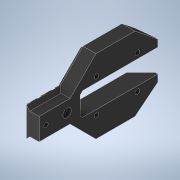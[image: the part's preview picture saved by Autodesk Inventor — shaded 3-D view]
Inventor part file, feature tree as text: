
AUTODESK INVENTOR PART (.ipt)
format: ipt  version: 2021 (Build 250183000, 183)  size: 281,600 bytes
history: native  units: mm
features: extrude x7, sketch x6, chamfer x3, projected_geometry x3, pattern_linear x1
ambient origin geometry x8: Origin, YZ Plane, XZ Plane, XY Plane, X Axis, Y Axis, Z Axis, Center Point
bodies: Solid1 (feature_tree)
feature tree (20):
  extrude  "Extrusion1"  Depth=29.0mm
  extrude  "Extrusion2"  Depth=12.0mm
  chamfer  "Chamfer3"  Distance=55.2mm
  chamfer  "Chamfer2"  Distance=29.2mm
  extrude  "Extrusion3"  Depth=10.0mm
  extrude  "Extrusion4"  Depth=10.0mm
  pattern_linear  "Rectangular Pattern1"  Spacing1=12.0mm  [1 undecoded]
  sketch  "Sketch5"  dims[d6=1.85mm]
  extrude  "Extrusion5"  Depth=18.0mm
  extrude  "Extrusion6"  Depth=10.0mm
  extrude  "Extrusion7"  Depth=10.0mm
  chamfer  "Chamfer5"  Distance=15.6718mm
  sketch  "Sketch1"  dims[d0=24.0mm d1=29.0mm]
  sketch  "Sketch2"  dims[d2=16.5mm d3=12.0mm]
  sketch  "Sketch3"  dims[d4=3.2mm]
  projected_geometry  "Projected Loop1"
  projected_geometry  "Projected Loop2"
  sketch  "Sketch4"  dims[d5=11.8mm]
  sketch  "Sketch6"  dims[d7=1.85mm d9=55.2mm d11=29.2mm d12=25.967009mm d13=32.0mm d14=12.0mm d15=0.0mm d16=18.0mm d17=5.0mm d19=24.668484mm d23=15.6718mm d29=15.67mm d30=2.76mm d32=10.15mm d33=2.77mm d34=2.77mm d35=3.78mm d36=0.0mm d37=20.0mm d38=80.0mm d40=22.0mm d41=0.0mm d42=2.77mm d43=2.0mm d44=45.0deg d45=18.41498mm d46=2.0mm d47=45.0deg d51=0.0mm d52=0.0mm d56=5.25mm d58=4.0mm d59=0.0mm d60=0.0mm d61=30.0mm d63=10.0mm d64=1.0mm d65=18.0mm d66=5.0mm d67=20.0mm d68=6.0mm d69=3.2mm d70=3.0mm d71=0.0mm d72=0.0mm d73=0.0mm d74=6.0mm d75=9.0mm d76=0.0mm d77=10.0mm d78=2.0mm d79=45.0deg]
  projected_geometry  "Projected Loop3"
note: 1 required parameter value undecoded (feature->parameter linkage not recoverable at this tier; creation-order binding heuristic only, values carry confidence <= 0.55)
